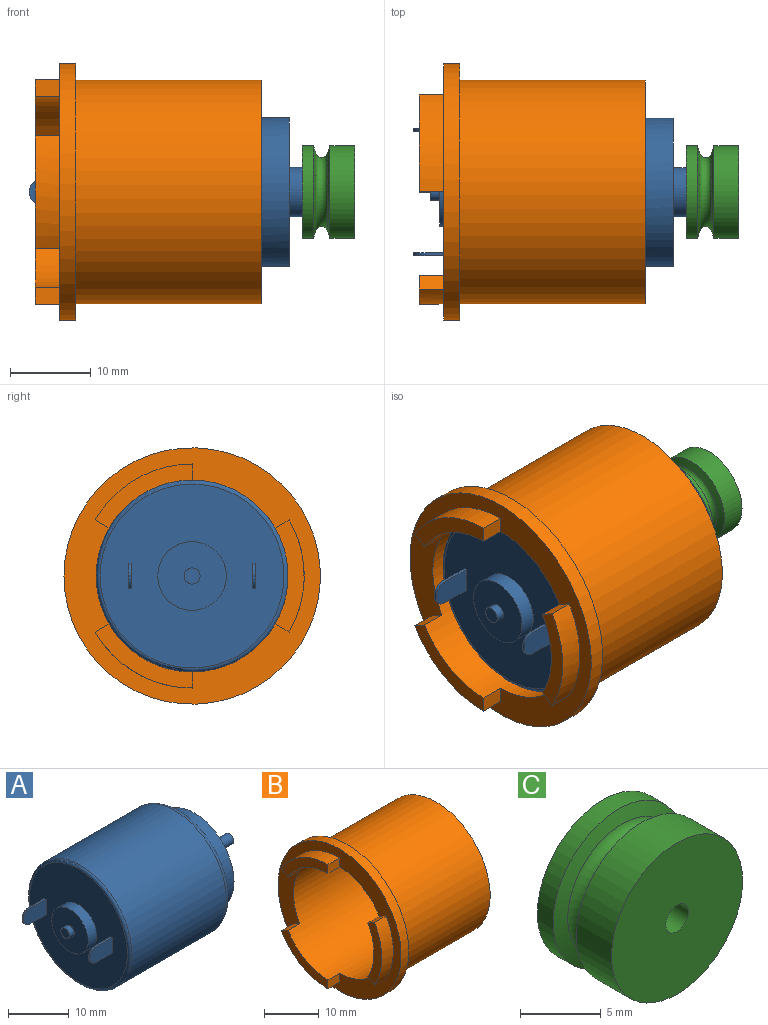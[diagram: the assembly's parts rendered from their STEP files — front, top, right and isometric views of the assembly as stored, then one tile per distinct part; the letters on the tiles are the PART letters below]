
ASSEMBLY  parts=3 mates=2
PART A: 29 faces, bbox 40.4x25.8x25.8 mm
  f0: plane 22.8x22.8mm, normal (-1,0,0), area 349.3mm2, adj f5,f9,f10,f11,f12,f13,f15,f16
  f1: plane 8.5x8.5mm, normal (-1,0,0), area 53.6mm2, adj f5,f6
  f2: cylinder r=11.9mm len=23.8mm, axis (-1,0,0), area 1644.9mm2, adj f8,f9
  f3: plane 21.8x21.8mm, normal (1,0,0), area 107.3mm2, adj f4,f8
  f4: cylinder r=9.2mm len=18.4mm, axis (-1,0,0), area 202.3mm2, adj f3,f28
  f5: cylinder r=4.25mm len=8.5mm, axis (1,0,0), area 53.4mm2, adj f0,f1
  f6: cylinder r=1mm len=2mm, axis (1,0,0), area 7mm2, adj f1,f7
  f7: plane 2x2mm, normal (-1,0,0), area 3.1mm2, adj f6
  f8: torus R=10.9mm, axis (-1,0,0), area 113.9mm2, adj f2,f3
  f9: torus R=11.4mm, axis (1,0,0), area 57.8mm2, adj f0,f2
  f10: plane 5.26x3.15mm, normal (0,1,0), area 15.6mm2, adj f0,f11,f13,f14,f22,f23
  f11: plane 3.76x0.35mm, normal (0,0,-1), area 1.3mm2, adj f0,f10,f12,f22
  f12: plane 5.26x3.15mm, normal (0,-1,0), area 15.6mm2, adj f0,f11,f13,f14,f22,f23
  f13: plane 3.76x0.35mm, normal (0,0,1), area 1.3mm2, adj f0,f10,f12,f23
  f14: plane 0.35x0.15mm, normal (-1,0,0), area 0.1mm2, adj f10,f12,f22,f23
  f15: plane 5.26x3.15mm, normal (0,1,0), area 15.6mm2, adj f0,f16,f18,f19,f20,f21
  f16: plane 3.76x0.35mm, normal (0,0,-1), area 1.3mm2, adj f0,f15,f17,f20
  f17: plane 5.26x3.15mm, normal (0,-1,0), area 15.6mm2, adj f0,f16,f18,f19,f20,f21
  f18: plane 3.76x0.35mm, normal (0,0,1), area 1.3mm2, adj f0,f15,f17,f21
  f19: plane 0.35x0.15mm, normal (-1,0,0), area 0.1mm2, adj f15,f17,f20,f21
  f20: cylinder r=1.5mm len=1.5mm, axis (0,1,0), area 0.8mm2, adj f15,f16,f17,f19
  f21: cylinder r=1.5mm len=1.5mm, axis (0,-1,0), area 0.8mm2, adj f15,f17,f18,f19
  f22: cylinder r=1.5mm len=1.5mm, axis (0,1,0), area 0.8mm2, adj f10,f11,f12,f14
  f23: cylinder r=1.5mm len=1.5mm, axis (0,-1,0), area 0.8mm2, adj f10,f12,f13,f14
  f24: plane 2x2mm, normal (1,0,0), area 3.1mm2, adj f25
  f25: cylinder r=1mm len=6.5mm, axis (-1,0,0), area 40.8mm2, adj f24,f26
  f26: plane 6.1x6.1mm, normal (1,0,0), area 26.1mm2, adj f25,f27
  f27: cylinder r=3.05mm len=6.1mm, axis (-1,0,0), area 30.7mm2, adj f26,f28
  f28: plane 18.4x18.4mm, normal (1,0,0), area 236.7mm2, adj f4,f27
PART B: 18 faces, bbox 28x31.8x31.8 mm
  f0: cylinder r=13.9mm len=12.04mm, axis (1,0,0), area 43.7mm2, adj f3,f4,f10,f17
  f1: cylinder r=11.9mm len=28mm, axis (1,0,0), area 1981.4mm2, adj f2,f3,f4,f5,f6,f7,f10,f14
  f2: plane 3x1.73mm, normal (0,0.5,0.87), area 6mm2, adj f1,f9,f10,f15
  f3: plane 3x1.73mm, normal (0,0.5,-0.87), area 6mm2, adj f0,f1,f10,f17
  f4: plane 3x2mm, normal (0,-1,0), area 6mm2, adj f0,f1,f10,f17
  f5: plane 3x1.73mm, normal (0,0.5,0.87), area 6mm2, adj f1,f8,f10,f16
  f6: plane 3x1.73mm, normal (0,0.5,-0.87), area 6mm2, adj f1,f8,f10,f16
  f7: plane 3x2mm, normal (0,-1,0), area 6mm2, adj f1,f9,f10,f15
  f8: cylinder r=13.9mm len=13.9mm, axis (1,0,0), area 43.7mm2, adj f5,f6,f10,f16
  f9: cylinder r=13.9mm len=12.04mm, axis (1,0,0), area 43.7mm2, adj f2,f7,f10,f15
  f10: plane 31.8x31.8mm, normal (-1,0,0), area 268.3mm2, adj f0,f1,f2,f3,f4,f5,f6,f7
  f11: cylinder r=15.9mm len=31.8mm, axis (1,0,0), area 199.8mm2, adj f10,f12
  f12: plane 31.8x31.8mm, normal (1,0,0), area 187.2mm2, adj f11,f13
  f13: cylinder r=13.9mm len=27.8mm, axis (1,0,0), area 2008.7mm2, adj f12,f14
  f14: plane 27.8x27.8mm, normal (1,0,0), area 162.1mm2, adj f1,f13
  f15: plane 12.05x7.95mm, normal (-1,0,0), area 27mm2, adj f1,f2,f7,f9
  f16: plane 13.91x3.6mm, normal (-1,0,0), area 27mm2, adj f1,f5,f6,f8
  f17: plane 12.04x7.95mm, normal (-1,0,0), area 27mm2, adj f0,f1,f3,f4
PART C: 8 faces, bbox 11.5x6.5x11.5 mm
  f0: torus R=5mm, axis (0,-1,0), area 52.9mm2, adj f1,f6
  f1: cone r=4.77mm half-angle=72.5deg, axis (0,1,0), area 33.8mm2, adj f0,f2
  f2: cylinder r=5.75mm len=11.5mm, axis (0,-1,0), area 49.8mm2, adj f1,f3
  f3: plane 11.5x11.5mm, normal (0,1,0), area 100.7mm2, adj f2,f7
  f4: plane 11.5x11.5mm, normal (0,-1,0), area 100.7mm2, adj f5,f7
  f5: cylinder r=5.75mm len=11.5mm, axis (0,-1,0), area 111.2mm2, adj f4,f6
  f6: cone r=4.77mm half-angle=72.5deg, axis (0,-1,0), area 33.8mm2, adj f0,f5
  f7: cylinder r=1mm len=6.5mm, axis (0,1,0), area 40.8mm2, adj f3,f4
PLACE A at identity
PLACE B at identity fixed
PLACE C rot(axis=(-0.58,0.58,0.58),120deg) t=(31,0,0)mm
MATE fastened C.f7 <-> A.f2  axis (1,0,0) through (35.1,0,0)mm
MATE fastened A.f2 <-> B.f0  axis (1,0,0) through (23.5,0,0)mm
